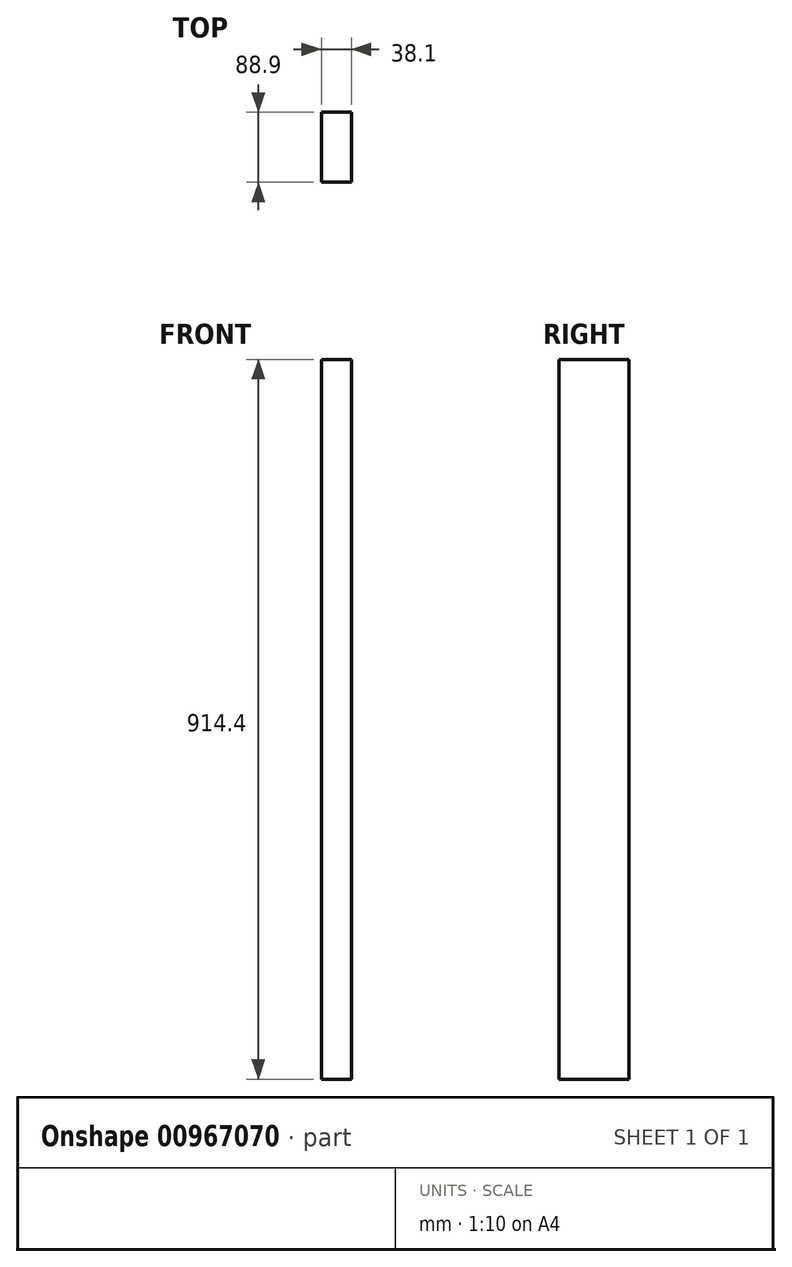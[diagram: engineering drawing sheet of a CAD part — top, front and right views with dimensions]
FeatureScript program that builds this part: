
annotation { "Feature Type Name" : "Feature", "Feature Type Description" : "" }
export const myFeature = defineFeature(function(context is Context, id is Id, definition is map)
    precondition{}
    {
        {
            var Q0;
            Q0=qCreatedBy(makeId("Top.planeOp"),FACE);
            var sketch = newSketch(context, id + "F0", { "sketchPlane" : qUnion([Q0])});
            skLineSegment(sketch, "E0.bottom", {"start": v(0, 0) * mm, "end": v(-38.1, 0) * mm});
            skLineSegment(sketch, "E0.top", {"start": v(0, 88.9) * mm, "end": v(-38.1, 88.9) * mm});
            skLineSegment(sketch, "E0.left", {"start": v(0, 0) * mm, "end": v(0, 88.9) * mm});
            skLineSegment(sketch, "E0.right", {"start": v(-38.1, 0) * mm, "end": v(-38.1, 88.9) * mm});
            skSolve(sketch);
        }
        {
            var Q0;
            Q0 = qSketchRegion(id + "F0", true);
            extrude(context, id + "F1", {"entities" : qUnion([Q0]), "depth" : 914.4 * mm, "offsetDistance" : 25.4 * mm});
        }
    });
